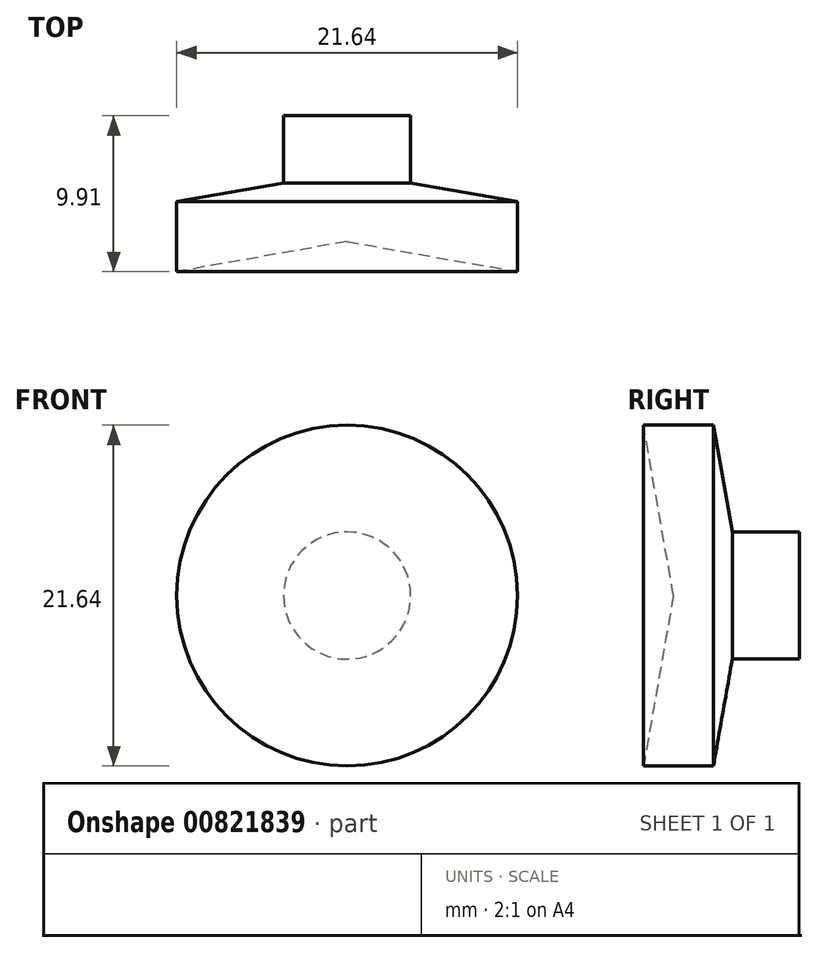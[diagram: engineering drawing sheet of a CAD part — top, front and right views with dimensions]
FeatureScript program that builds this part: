
annotation { "Feature Type Name" : "Feature", "Feature Type Description" : "" }
export const myFeature = defineFeature(function(context is Context, id is Id, definition is map)
    precondition{}
    {
        {
            var Q0;
            Q0=qCreatedBy(makeId("Right.planeOp"),FACE);
            var sketch = newSketch(context, id + "F0", { "sketchPlane" : qUnion([Q0])});
            skLineSegment(sketch, "E0", {"start": v(-76.2, 0) * mm, "end": v(76.41, 0) * mm});
            skLineSegment(sketch, "E1", {"start": v(0, 0) * mm, "end": v(-1.9, 10.82) * mm});
            skLineSegment(sketch, "E2", {"start": v(-1.9, 10.82) * mm, "end": v(2.54, 10.82) * mm});
            skLineSegment(sketch, "E3", {"start": v(2.54, 10.82) * mm, "end": v(4.45, 0) * mm});
            skLineSegment(sketch, "E4", {"start": v(4.45, 0) * mm, "end": v(7.94, 0) * mm});
            skSolve(sketch);
        }
        {
            var Q0;
            {var subQ0=sQuery(id+"F0.wireOp",EDGE,"E1");Q0=makeQuery(id+"F0.imprint","IMPRINT",FACE,{"disambiguationData":[TD([[makeQuery(id+"F0.imprint","IMPRINT",EDGE,{"derivedFrom":subQ0}),-1.0]])]});}
            var Q1;
            Q1=sQuery(id+"F0.wireOp",EDGE,"E0");
            revolve(context, id + "F1", {"surfaceOperationType" : NewSurfaceOperationType.NEW, "entities" : qUnion([Q0]), "axis" : qUnion([Q1]), "revolveType" : RevolveType.FULL});
        }
        {
            var Q0;
            Q0=qCreatedBy(makeId("Front.planeOp"),FACE);
            var sketch = newSketch(context, id + "F2", { "sketchPlane" : qUnion([Q0])});
            skCircle(sketch, "E5", {"center": v(0, 0) * mm, "radius": 4.04 * mm});
            skSolve(sketch);
        }
        {
            var Q0;
            Q0 = qSketchRegion(id + "F2", true);
            extrude(context, id + "F3", {"entities" : qUnion([Q0]), "operationType" : NewBodyOperationType.ADD, "oppositeDirection" : true, "depth" : 3.5 * mm, "offsetDistance" : 25.4 * mm});
        }
        {
            var Q0;
            Q0=makeQuery(id+"F2.imprint","IMPRINT",FACE,{"disambiguationData":[TD([[makeQuery(id+"F2.imprint","IMPRINT",EDGE,{"derivedFrom":sQuery(id+"F2.wireOp",EDGE,"E5")}),1.0]])]});
            var Q1;
            Q1=sQuery(id+"F2.wireOp",EDGE,"E5");
            extrude(context, id + "F4", {"entities" : qUnion([Q0]), "operationType" : NewBodyOperationType.ADD, "surfaceEntities" : qUnion([Q1]), "oppositeDirection" : true, "depth" : 8 * mm, "offsetDistance" : 25.4 * mm});
        }
    });
